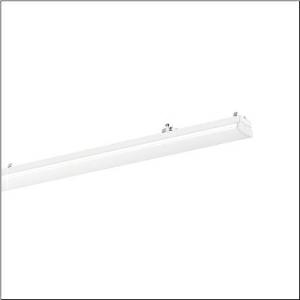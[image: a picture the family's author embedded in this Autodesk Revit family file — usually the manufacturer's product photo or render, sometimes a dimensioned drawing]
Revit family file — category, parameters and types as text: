
# Revit family: licross_11_recessed_opal_mo_51te1ddn495g
name_source: partatom
category: Lighting Fixtures
units: mm (PartAtom-declared; Revit-internal decimal feet)

## family parameters
Cut with Voids When Loaded = No
Host = Face
Light Source = No
Part Type = Normal
Room Calculation Point = No
Round Connector Dimension = Use Diameter
Shared = No

## types (1)
- --- (1 x LED, 9710 lm, 56.7 W, 4000K)
    Apparent Load = 57 VA
    CIE Flux Codes = 44 73 91 87 100
    Color Rendering = 80
    Color Temperature = 4000K
    Default Elevation = 1800 mm
    Description = Licross 11 recessed opal MO, luminaire insert, of sheet steel, coil coated, white, length: 1.500mm, width: 76mm, height: 87mm, LED rated luminous flux: 9.710lm, light colour: 840, SDCM (Standard Deviation of Colour Matching)MacAdam ≤ 2 SDCM (initial), control gear: DALI 2, with plug, 5-pole, with phase selection, mains connection: 220..240V, AC, 50/60Hz, rated input power: 57W, internal wiring halogen-free, primary optical cover: cover, of PMMA, light emission: direct with ceiling illumination distribution, primary light characteristic: symmetric, protection rating (complete): IP54, insulation class (complete): insulation class I (protective earthing), certification: CE, ENEC, VDE, UKCA, protection symbol: D if used in an environment with non-conductive dust loads with corresponding accessories, impact resistance: IK06, permissible ambient temperature for indoor applications: -25..+35°C, corresponds to IFS (International Featured Standards) requirements for safety and quality in the food industry, reducing of maximum allowable ambient temperature of 5°C with ceiling mounting, LABS conformity tested according to VDMA 24364:2018-05, The light source and the operating device comply with the requirements of the Ecodesign Regulation (EU) 2019/2020 and are replaceable in accordance with this regulation, packaging unit: 1 piece
    Height = 83 mm
    Lamp = 1 x LED
    Lamp Light Flux = 9710 lm
    Lamp Power = 56.7 W
    Lamp count = 1
    Length = 1500 mm
    Luminous efficacy = 171 lm/W
    Manufacturer = Siteco
    ModVariant = No
    Model = 51TE1DDN495G
    Mounting Place = Ceiling
    Mounting Type = Pendant
    Number of Poles = 1
    OnlyDefault = Yes
    Power Factor = 1
    Product Name = Licross 11 recessed opal MO
    Product group = luminaire insert | ceiling pendant
    ProductGroupID = 901
    Protection Class = Protection class I
    Protection Degree = IP 54
    RLX_Detail_Level = 1
    RLX_Emergency_Light_Flux = 0 lm
    RLX_Emergency_Type = 0
    RLX_Emergency_Type_DB = No
    RlxData = <blob elided: 27105 chars, md5=643c6ad5>
    Socket = socket
    Standby Power = 0 W
    System Light Flux = 9710 lm
    System Power = 57 W
    Type Comments = factory setting: luminous flux: 100 % | dim-lin: 254 | 378 mA
    Type Image = l_1313666.jpg
    URL = http://relux.com
    VarID = @adj_083687
    Voltage = 0 V
    Weight = 0.00 kg
    Width = 76 mm

## geometry (parser evidence)
native form markers: Blend x4, Sweep x13
no freeform markers — native parametric forms only
